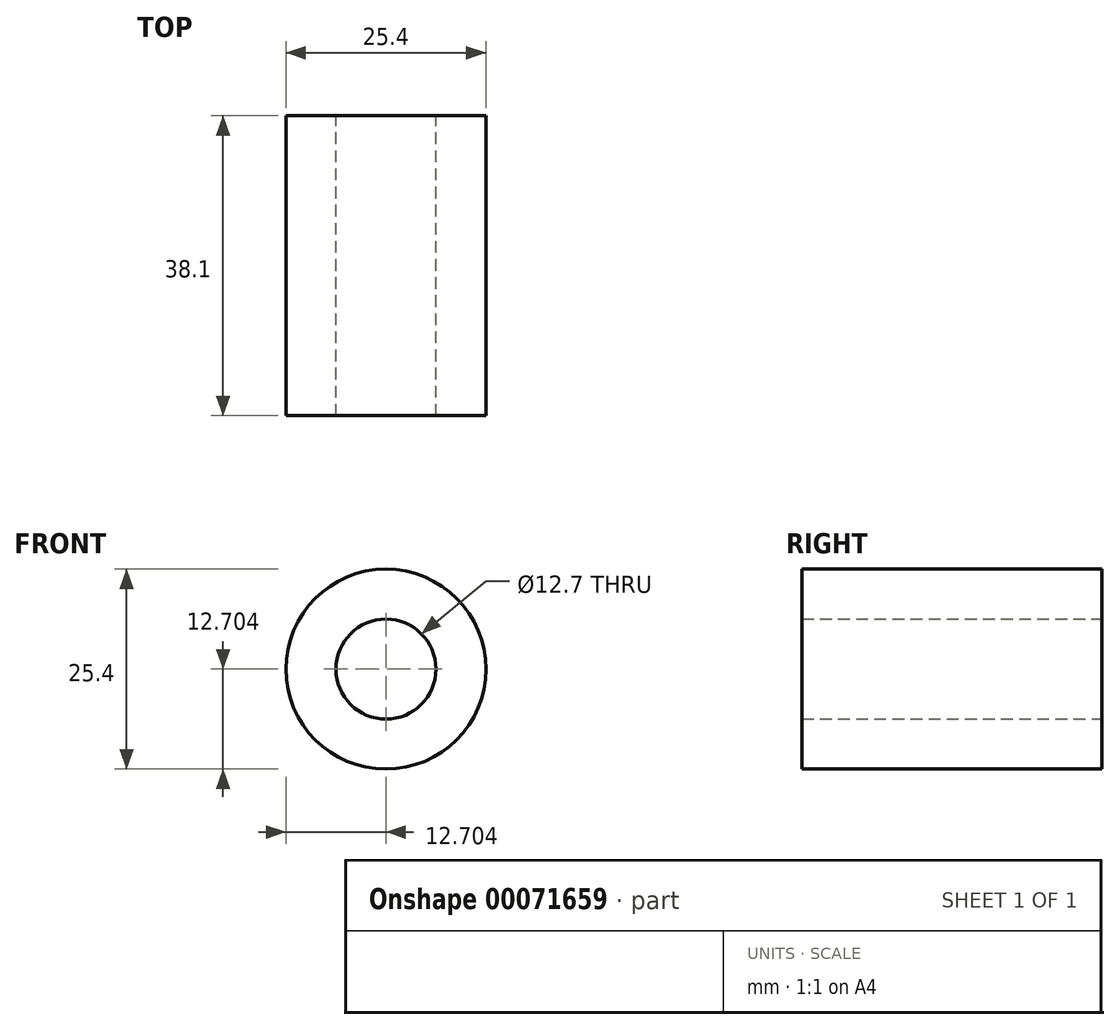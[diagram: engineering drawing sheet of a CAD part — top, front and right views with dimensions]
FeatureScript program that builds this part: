
annotation { "Feature Type Name" : "Feature", "Feature Type Description" : "" }
export const myFeature = defineFeature(function(context is Context, id is Id, definition is map)
    precondition{}
    {
        {
            var Q0;
            Q0=qCreatedBy(makeId("Front.planeOp"),FACE);
            var sketch = newSketch(context, id + "F0", { "sketchPlane" : qUnion([Q0])});
            skCircle(sketch, "E0", {"center": v(-67.6, 36.64) * mm, "radius": 12.7 * mm});
            skCircle(sketch, "E1", {"center": v(-67.6, 36.64) * mm, "radius": 6.35 * mm});
            skSolve(sketch);
        }
        {
            var Q0;
            Q0=makeQuery(id+"F0.imprint","IMPRINT",FACE,{"disambiguationData":[TD([[makeQuery(id+"F0.imprint","IMPRINT",EDGE,{"derivedFrom":sQuery(id+"F0.wireOp",EDGE,"E0")}),1.0]])]});
            extrude(context, id + "F1", {"entities" : qUnion([Q0]), "depth" : 38.1 * mm});
        }
    });
